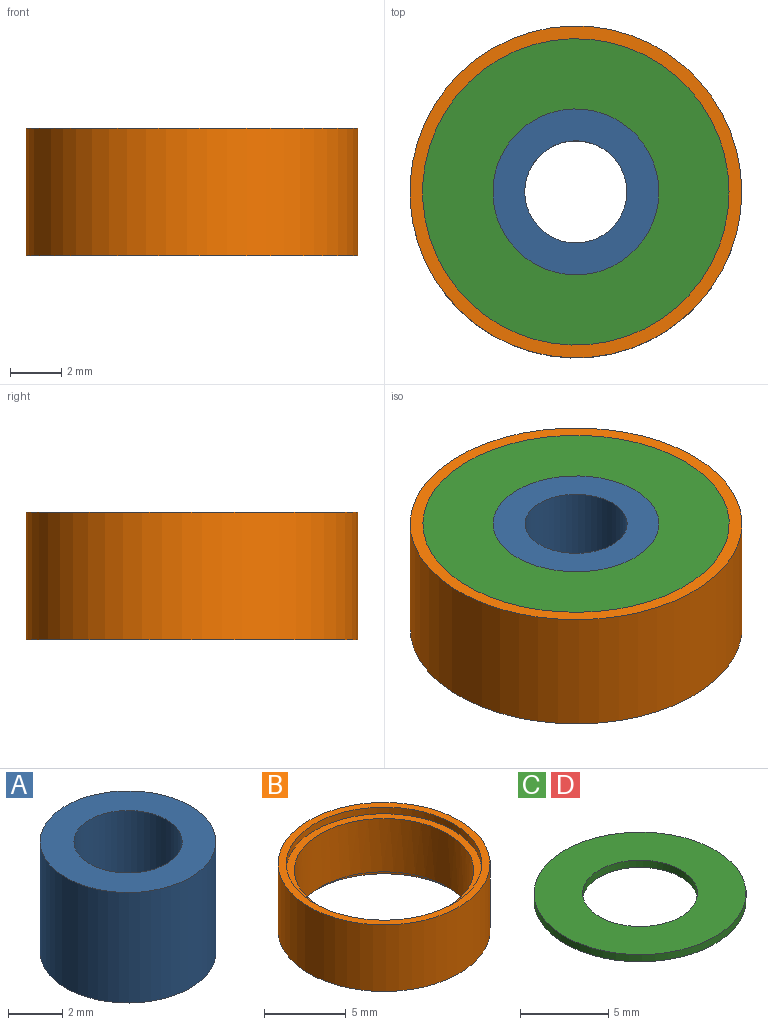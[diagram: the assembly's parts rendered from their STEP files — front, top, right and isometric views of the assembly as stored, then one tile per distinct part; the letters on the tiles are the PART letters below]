
ASSEMBLY  parts=4 mates=3
PART A: 4 faces, bbox 6.5x6.5x5 mm
  f0: cylinder r=2mm len=5mm, axis (0,0,-1), area 62.8mm2, adj f2,f3
  f1: cylinder r=3.25mm len=6.5mm, axis (0,0,-1), area 102.1mm2, adj f2,f3
  f2: plane 6.5x6.5mm, normal (0,0,1), area 20.6mm2, adj f0,f1
  f3: plane 6.5x6.5mm, normal (0,0,-1), area 20.6mm2, adj f0,f1
PART B: 8 faces, bbox 13x13x5 mm
  f0: cylinder r=5.5mm len=11mm, axis (0,0,-1), area 138.2mm2, adj f5,f7
  f1: cylinder r=6.5mm len=13mm, axis (0,0,-1), area 204.2mm2, adj f2,f3
  f2: plane 13x13mm, normal (0,0,1), area 19.6mm2, adj f1,f4
  f3: plane 13x13mm, normal (0,0,-1), area 19.6mm2, adj f1,f6
  f4: cylinder r=6mm len=12mm, axis (0,0,1), area 18.8mm2, adj f2,f5
  f5: plane 12x12mm, normal (0,0,1), area 18.1mm2, adj f0,f4
  f6: cylinder r=6mm len=12mm, axis (0,0,-1), area 18.8mm2, adj f3,f7
  f7: plane 12x12mm, normal (0,0,-1), area 18.1mm2, adj f0,f6
PART C: 4 faces, bbox 12x12x0.5 mm
  f0: cylinder r=3.25mm len=6.5mm, axis (0,0,-1), area 10.2mm2, adj f2,f3
  f1: cylinder r=6mm len=12mm, axis (0,0,-1), area 18.8mm2, adj f2,f3
  f2: plane 12x12mm, normal (0,0,1), area 79.9mm2, adj f0,f1
  f3: plane 12x12mm, normal (0,0,-1), area 79.9mm2, adj f0,f1
PART D: same geometry as C
PLACE A at identity
PLACE B at identity
PLACE C t=(0,0,4.5)mm
PLACE D at identity
MATE fastened D.f1 <-> B.f6  axis (0,0,1) through (0,0,0.5)mm
MATE revolute A.f1 <-> B.f6  axis (0,0,-1) through (0,0,0)mm
MATE fastened C.f1 <-> B.f4  axis (0,0,-1) through (0,0,4.5)mm
